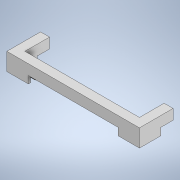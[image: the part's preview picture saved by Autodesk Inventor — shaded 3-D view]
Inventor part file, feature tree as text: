
AUTODESK INVENTOR PART (.ipt)
format: ipt  version: 2022 (Build 260153000, 153)  size: 240,640 bytes
history: native  units: in
note: dims shown in document units (in); Inventor stores cm internally (conversion verified against a paired STEP export)
features: projected_geometry x4, extrude x3, sketch x1
ambient origin geometry x8: Origin, YZ Plane, XZ Plane, XY Plane, X Axis, Y Axis, Z Axis, Center Point
bodies: Solid1 (feature_tree)
feature tree (8):
  extrude  "Extrusion1"  Depth=0.124in
  extrude  "Extrusion2"  Depth=0.3937in
  extrude  "Extrusion3"  Depth=0.3937in
  sketch  "Sketch1"  dims[d0=0.124in d1=0.124in d2=0.7874in d3=0.7874in d4=0.0591in d5=0.0591in d6=0.1969in d7=0.0in d8=0.0787in d9=0.0in d10=0.3937in d11=0.3937in d12=0.5768in d13=0.5768in d14=0.1969in d15=0.0in d16=3.4488in d17=0.0in d18=0.0in d19=0.7874in d20=0.0591in d21=0.124in d22=0.0in d23=0.0in d24=0.0in d25=0.0in d26=0.0591in d27=0.0591in d28=0.5768in d29=0.5768in d30=0.3937in d31=0.0in d32=0.0in d33=0.0in]
  projected_geometry  "Projected Loop1"
  projected_geometry  "Projected Loop2"
  projected_geometry  "Projected Loop3"
  projected_geometry  "Projected Loop4"
